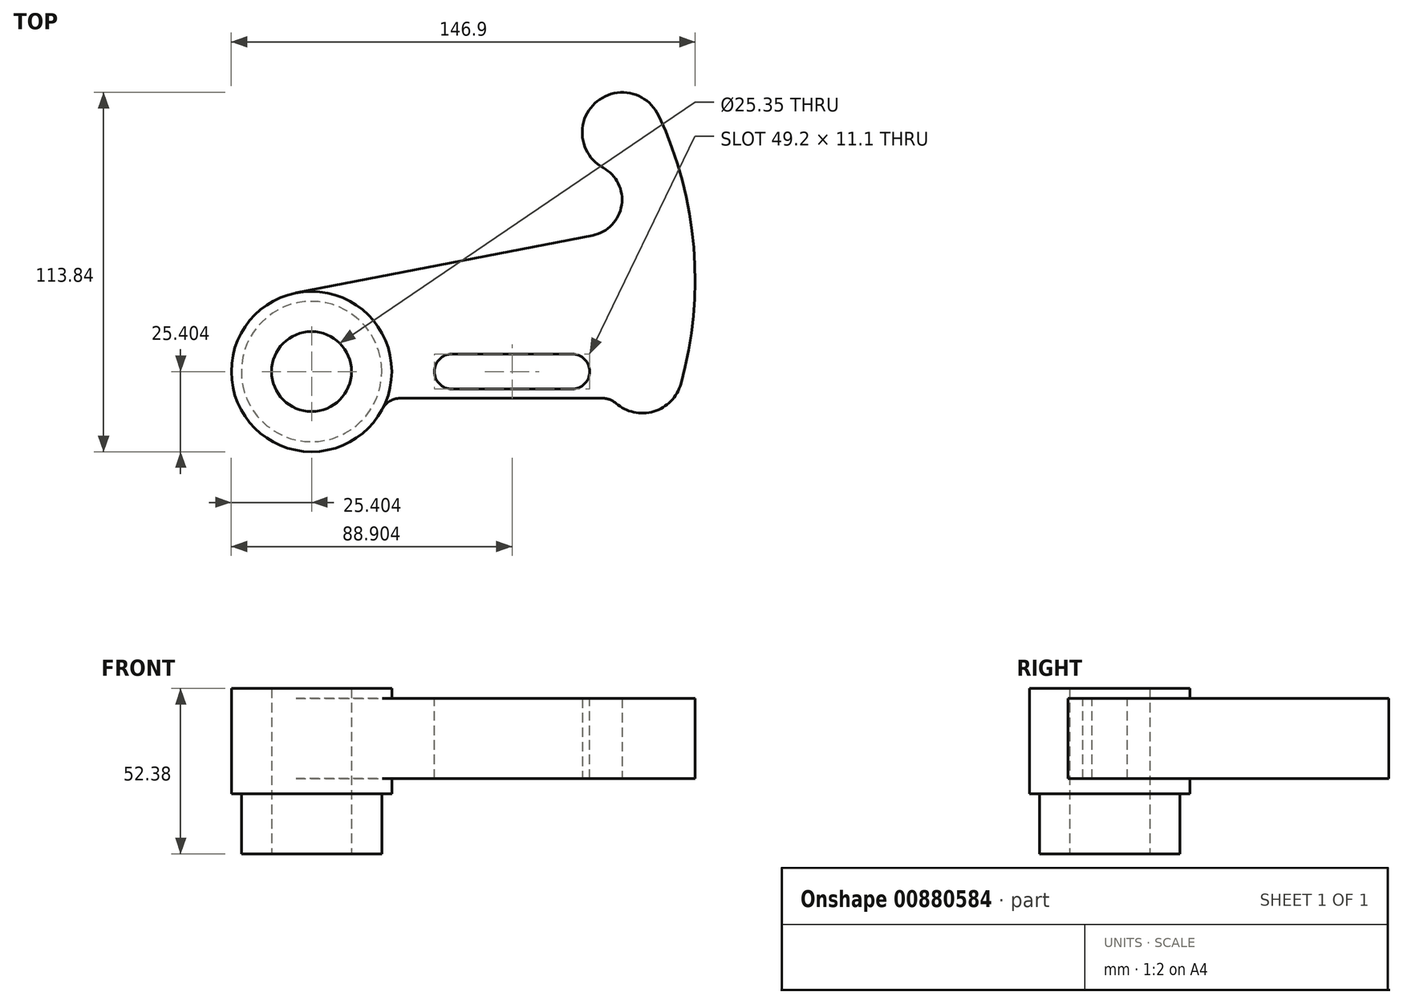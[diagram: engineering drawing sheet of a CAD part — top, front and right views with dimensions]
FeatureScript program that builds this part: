
annotation { "Feature Type Name" : "Feature", "Feature Type Description" : "" }
export const myFeature = defineFeature(function(context is Context, id is Id, definition is map)
    precondition{}
    {
        {
            var Q0;
            Q0=qCreatedBy(makeId("Top.planeOp"),FACE);
            var sketch = newSketch(context, id + "F0", { "sketchPlane" : qUnion([Q0])});
            skArc(sketch, "E0", {"start": v(-100.94, 5) * mm, "mid": v(-115.34, -36.5) * mm, "end": v(-72.15, -28.4) * mm});
            skLineSegment(sketch, "E1", {"start": v(-100.94, 5) * mm, "end": v(-7.06, 23.26) * mm});
            skLineSegment(sketch, "E2", {"start": v(-100.94, 5) * mm, "end": v(-19.7, 5) * mm, "construction": true});
            skArc(sketch, "E3", {"start": v(17.83, -29.17) * mm, "mid": v(12.37, 16.12) * mm, "end": v(-10.37, 55.68) * mm, "construction": true});
            skArc(sketch, "E4", {"start": v(-7.06, 23.26) * mm, "mid": v(2.11, 32.8) * mm, "end": v(-3.75, 44.66) * mm});
            skArc(sketch, "E5", {"start": v(0.3, -29.97) * mm, "mid": v(12.3, -32.56) * mm, "end": v(20.89, -23.8) * mm});
            skLineSegment(sketch, "E6.MirrorCS", {"start": v(-72.15, -28.4) * mm, "end": v(-3.87, -28.4) * mm});
            skArc(sketch, "E7", {"start": v(0.3, -29.97) * mm, "mid": v(-1.64, -28.8) * mm, "end": v(-3.87, -28.4) * mm});
            skPoint(sketch, "E8.endSnap0", {"position": v(13.83, 61.2) * mm});
            skArc(sketch, "E9.trimOffspring", {"start": v(13.83, 61.2) * mm, "mid": v(-6.37, 65.06) * mm, "end": v(-3.75, 44.66) * mm});
            skArc(sketch, "E10", {"start": v(20.89, -23.8) * mm, "mid": v(24.98, 19.33) * mm, "end": v(13.83, 61.2) * mm});
            skPoint(sketch, "E11.orphan", {"position": v(0, 30.87) * mm});
            skSolve(sketch);
        }
        {
            var Q0;
            Q0=makeQuery(id+"F0.imprint","IMPRINT",FACE,{"disambiguationData":[TD([[makeQuery(id+"F0.imprint","IMPRINT",EDGE,{"derivedFrom":sQuery(id+"F0.wireOp",EDGE,"E0")}),1.0]])]});
            extrude(context, id + "F1", {"entities" : qUnion([Q0]), "depth" : 25.4 * mm, "offsetDistance" : 25.4 * mm});
        }
        {
            var Q0;
            Q0=makeQuery(id+"F1.opExtrude","CAP_FACE",FACE,{"disambiguationData":[OSD([sQuery(id+"F0.wireOp",EDGE,"E0"),sQuery(id+"F0.wireOp",EDGE,"E1"),sQuery(id+"F0.wireOp",EDGE,"E4"),sQuery(id+"F0.wireOp",EDGE,"E5"),sQuery(id+"F0.wireOp",EDGE,"E6.MirrorCS"),sQuery(id+"F0.wireOp",EDGE,"E7"),sQuery(id+"F0.wireOp",EDGE,"E9.trimOffspring"),sQuery(id+"F0.wireOp",EDGE,"E10")])],"isStart":false});
            var sketch = newSketch(context, id + "F2", { "sketchPlane" : qUnion([Q0])});
            skCircle(sketch, "E12", {"center": v(-96.1, -19.93) * mm, "radius": 25.4 * mm});
            skSolve(sketch);
        }
        {
            var Q0;
            Q0 = qSketchRegion(id + "F2", true);
            extrude(context, id + "F3", {"entities" : qUnion([Q0]), "operationType" : NewBodyOperationType.ADD, "depth" : 3.17 * mm, "offsetDistance" : 25.4 * mm});
        }
        {
            var Q0;
            Q0=makeQuery(id+"F1.opExtrude","CAP_FACE",FACE,{"disambiguationData":[OSD([sQuery(id+"F0.wireOp",EDGE,"E0"),sQuery(id+"F0.wireOp",EDGE,"E1"),sQuery(id+"F0.wireOp",EDGE,"E4"),sQuery(id+"F0.wireOp",EDGE,"E5"),sQuery(id+"F0.wireOp",EDGE,"E6.MirrorCS"),sQuery(id+"F0.wireOp",EDGE,"E7"),sQuery(id+"F0.wireOp",EDGE,"E9.trimOffspring"),sQuery(id+"F0.wireOp",EDGE,"E10")])],"isStart":true});
            var sketch = newSketch(context, id + "F4", { "sketchPlane" : qUnion([Q0])});
            skCircle(sketch, "E13", {"center": v(-96.1, 19.93) * mm, "radius": 25.4 * mm});
            skSolve(sketch);
        }
        {
            var Q0;
            Q0 = qSketchRegion(id + "F4", true);
            extrude(context, id + "F5", {"entities" : qUnion([Q0]), "operationType" : NewBodyOperationType.ADD, "depth" : 4.75 * mm, "offsetDistance" : 25.4 * mm});
        }
        {
            var Q0;
            Q0=makeQuery(id+"F5.opExtrude","CAP_FACE",FACE,{"disambiguationData":[OSD([sQuery(id+"F4.wireOp",EDGE,"E13")])],"isStart":false});
            var sketch = newSketch(context, id + "F6", { "sketchPlane" : qUnion([Q0])});
            skCircle(sketch, "E14", {"center": v(-96.1, 19.93) * mm, "radius": 22.23 * mm});
            skSolve(sketch);
        }
        {
            var Q0;
            Q0 = qSketchRegion(id + "F6", true);
            extrude(context, id + "F7", {"entities" : qUnion([Q0]), "operationType" : NewBodyOperationType.ADD, "depth" : 19.05 * mm, "offsetDistance" : 25.4 * mm});
        }
        {
            var Q0;
            Q0=makeQuery(id+"F7.opExtrude","CAP_FACE",FACE,{"disambiguationData":[OSD([sQuery(id+"F6.wireOp",EDGE,"E14")])],"isStart":false});
            var sketch = newSketch(context, id + "F8", { "sketchPlane" : qUnion([Q0])});
            skCircle(sketch, "E15", {"center": v(-96.1, 19.93) * mm, "radius": 12.67 * mm});
            skSolve(sketch);
        }
        {
            var Q0;
            Q0 = qSketchRegion(id + "F8", true);
            extrude(context, id + "F9", {"entities" : qUnion([Q0]), "operationType" : NewBodyOperationType.REMOVE, "oppositeDirection" : true, "depth" : 74.17 * mm, "offsetDistance" : 25.4 * mm});
        }
        {
            var Q0;
            Q0=makeQuery(id+"F1.opExtrude","CAP_FACE",FACE,{"disambiguationData":[OSD([sQuery(id+"F0.wireOp",EDGE,"E0"),sQuery(id+"F0.wireOp",EDGE,"E1"),sQuery(id+"F0.wireOp",EDGE,"E4"),sQuery(id+"F0.wireOp",EDGE,"E5"),sQuery(id+"F0.wireOp",EDGE,"E6.MirrorCS"),sQuery(id+"F0.wireOp",EDGE,"E7"),sQuery(id+"F0.wireOp",EDGE,"E9.trimOffspring"),sQuery(id+"F0.wireOp",EDGE,"E10")])],"isStart":false});
            var sketch = newSketch(context, id + "F10", { "sketchPlane" : qUnion([Q0])});
            skLineSegment(sketch, "E16", {"start": v(-96.1, -19.93) * mm, "end": v(-25.24, -19.93) * mm, "construction": true});
            skLineSegment(sketch, "E17.bottom", {"start": v(-13.55, -25.48) * mm, "end": v(-51.65, -25.48) * mm});
            skLineSegment(sketch, "E17.top", {"start": v(-13.55, -14.38) * mm, "end": v(-51.65, -14.38) * mm});
            skPoint(sketch, "E17.middle", {"position": v(-32.6, -19.93) * mm});
            skArc(sketch, "E18", {"start": v(-51.65, -14.38) * mm, "mid": v(-57.2, -19.93) * mm, "end": v(-51.65, -25.48) * mm});
            skArc(sketch, "E19", {"start": v(-13.55, -25.48) * mm, "mid": v(-8, -19.93) * mm, "end": v(-13.55, -14.38) * mm});
            skSolve(sketch);
        }
        {
            var Q0;
            Q0 = qSketchRegion(id + "F10", true);
            extrude(context, id + "F11", {"entities" : qUnion([Q0]), "operationType" : NewBodyOperationType.REMOVE, "oppositeDirection" : true, "depth" : 43.69 * mm, "offsetDistance" : 25.4 * mm});
        }
        {
            var Q0;
            Q0=makeQuery(id+"F1.opExtrude","SWEPT_EDGE",EDGE,{"disambiguationData":[OSD([sQuery(id+"F0.wireOp",EDGE,"E0"),sQuery(id+"F0.wireOp",EDGE,"E6.MirrorCS")])]});
            fillet(context, id + "F12", {"entities" : qUnion([Q0]), "radius" : 6.35 * mm, "tangentPropagation" : true, "allowEdgeOverflow" : false});
        }
    });
